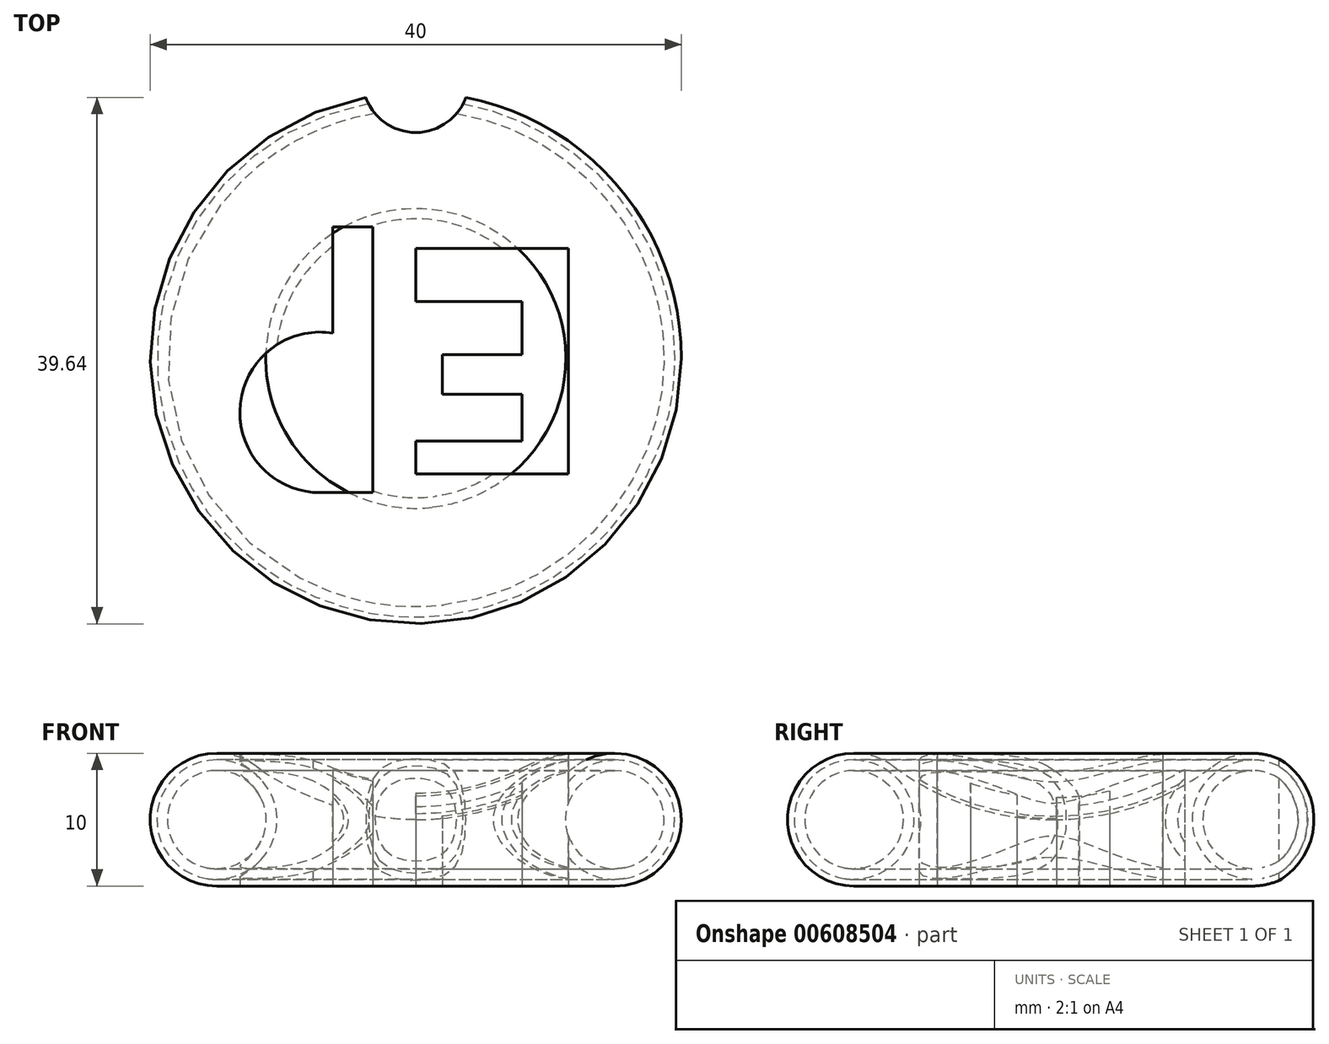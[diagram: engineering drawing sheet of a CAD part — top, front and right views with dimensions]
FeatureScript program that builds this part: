
annotation { "Feature Type Name" : "Feature", "Feature Type Description" : "" }
export const myFeature = defineFeature(function(context is Context, id is Id, definition is map)
    precondition{}
    {
        {
            var Q0;
            Q0=qCreatedBy(makeId("Front.planeOp"),FACE);
            var sketch = newSketch(context, id + "F0", { "sketchPlane" : qUnion([Q0])});
            skArc(sketch, "E0", {"start": v(-12, 9) * mm, "mid": v(-6.32, 6.03) * mm, "end": v(0, 5) * mm});
            skArc(sketch, "E1", {"start": v(-12, 9) * mm, "mid": v(-19.74, 6.58) * mm, "end": v(-15, 0) * mm});
            skLineSegment(sketch, "E2", {"start": v(0, 5) * mm, "end": v(0, 0) * mm});
            skLineSegment(sketch, "E3", {"start": v(0, 0) * mm, "end": v(-15, 0) * mm});
            skSolve(sketch);
        }
        {
            var Q0;
            Q0=makeQuery(id+"F0.imprint","IMPRINT",FACE,{"disambiguationData":[TD([[makeQuery(id+"F0.imprint","IMPRINT",EDGE,{"derivedFrom":sQuery(id+"F0.wireOp",EDGE,"E0")}),-1.0]])]});
            var Q1;
            Q1=sQuery(id+"F0.wireOp",EDGE,"E2");
            revolve(context, id + "F1", {"entities" : qUnion([Q0]), "axis" : qUnion([Q1]), "revolveType" : RevolveType.FULL});
        }
        {
            var Q0;
            Q0=makeQuery(id+"F1.opRevolve","SWEPT_FACE",FACE,{"disambiguationData":[OSD([sQuery(id+"F0.wireOp",EDGE,"E3")])]});
            var sketch = newSketch(context, id + "F2", { "sketchPlane" : qUnion([Q0])});
            skLineSegment(sketch, "E4", {"start": v(-3.25, -9.9) * mm, "end": v(-3.25, 10.1) * mm});
            skLineSegment(sketch, "E5", {"start": v(-3.25, 10.1) * mm, "end": v(-6.25, 10.1) * mm});
            skLineSegment(sketch, "E6", {"start": v(-6.25, -1.9) * mm, "end": v(-6.25, -9.9) * mm});
            skLineSegment(sketch, "E7", {"start": v(-3.25, -9.9) * mm, "end": v(-6.25, -9.9) * mm});
            skLineSegment(sketch, "E8", {"start": v(-6.25, 10.1) * mm, "end": v(-7.75, 10.1) * mm});
            skArc(sketch, "E9", {"start": v(-7.75, 10.1) * mm, "mid": v(-13.2, 3.32) * mm, "end": v(-6.25, -1.9) * mm});
            skLineSegment(sketch, "E10", {"start": v(11.5, 8.73) * mm, "end": v(11.5, -8.27) * mm});
            skLineSegment(sketch, "E11", {"start": v(0, -8.27) * mm, "end": v(11.5, -8.27) * mm});
            skLineSegment(sketch, "E12", {"start": v(0, -8.27) * mm, "end": v(0, -4.27) * mm});
            skLineSegment(sketch, "E13", {"start": v(0, -4.27) * mm, "end": v(8, -4.27) * mm});
            skLineSegment(sketch, "E14", {"start": v(8, -4.27) * mm, "end": v(8, -0.27) * mm});
            skLineSegment(sketch, "E15", {"start": v(8, -0.27) * mm, "end": v(2, -0.27) * mm});
            skLineSegment(sketch, "E16", {"start": v(2, 2.73) * mm, "end": v(2, -0.27) * mm});
            skLineSegment(sketch, "E17", {"start": v(2, 2.73) * mm, "end": v(8, 2.73) * mm});
            skLineSegment(sketch, "E18", {"start": v(8, 6.23) * mm, "end": v(8, 2.73) * mm});
            skLineSegment(sketch, "E19", {"start": v(8, 6.23) * mm, "end": v(0, 6.23) * mm});
            skLineSegment(sketch, "E20", {"start": v(11.5, 8.73) * mm, "end": v(0, 8.73) * mm});
            skLineSegment(sketch, "E21", {"start": v(0, 8.73) * mm, "end": v(0, 6.23) * mm});
            skPoint(sketch, "E22.orphan", {"position": v(0, -0.27) * mm});
            skSolve(sketch);
        }
        {
            var Q0;
            Q0=makeQuery(id+"F2.imprint","IMPRINT",FACE,{"disambiguationData":[TD([[makeQuery(id+"F2.imprint","IMPRINT",EDGE,{"derivedFrom":sQuery(id+"F2.wireOp",EDGE,"E4")}),1.0]])]});
            var Q1;
            Q1=makeQuery(id+"F2.imprint","IMPRINT",FACE,{"disambiguationData":[TD([[makeQuery(id+"F2.imprint","IMPRINT",EDGE,{"derivedFrom":sQuery(id+"F2.wireOp",EDGE,"bYQDJKkg-T13d-azlY-E3zt-dDLmTT6hyBzi")}),-1.0]])]});
            var Q2;
            {var subQ0=sQuery(id+"F2.wireOp",EDGE,"GuACwf4x-50aZ-0oHN-BAbR-x8a28NAcBo0e");var subQ1=sQuery(id+"F2.wireOp",EDGE,"7OYxP0y7-SmuM-tV8H-ZwjT-pEX8pjBidrrm");var subQ2=makeQuery(id+"F2.imprint","INTERSECT",VERTEX,{"derivedFrom":[subQ1,subQ0]});Q2=makeQuery(id+"F2.imprint","IMPRINT",FACE,{"disambiguationData":[TD([[makeQuery(id+"F2.imprint","IMPRINT",EDGE,{"disambiguationData":[TD([[subQ2,1.0]])],"derivedFrom":subQ1}),-1.0]])]});}
            extrude(context, id + "F3", {"entities" : qUnion([Q0, Q1, Q2]), "operationType" : NewBodyOperationType.REMOVE, "oppositeDirection" : true, "depth" : 25 * mm, "offsetDistance" : 25 * mm});
        }
        {
            var Q0;
            Q0=qCreatedBy(makeId("Front.planeOp"),FACE);
            var sketch = newSketch(context, id + "F4", { "sketchPlane" : qUnion([Q0])});
            skCircle(sketch, "E23", {"center": v(-15, 5) * mm, "radius": 4.5 * mm});
            skCircle(sketch, "E24", {"center": v(-15, 5) * mm, "radius": 3.7 * mm});
            skSolve(sketch);
        }
        {
            var Q0;
            Q0=sQuery(id+"F4.wireOp",EDGE,"E24");
            var Q1;
            Q1=sQuery(id+"F0.wireOp",EDGE,"E2");
            revolve(context, id + "F5", {"bodyType" : ToolBodyType.SURFACE, "surfaceEntities" : qUnion([Q0]), "axis" : qUnion([Q1]), "revolveType" : RevolveType.FULL});
        }
        {
            var Q0;
            Q0=qCreatedBy(makeId("Top.planeOp"),FACE);
            var sketch = newSketch(context, id + "F6", { "sketchPlane" : qUnion([Q0])});
            skCircle(sketch, "E25", {"center": v(0, 21) * mm, "radius": 4 * mm});
            skSolve(sketch);
        }
        {
            var Q0;
            Q0=makeQuery(id+"F6.imprint","IMPRINT",FACE,{"disambiguationData":[TD([[makeQuery(id+"F6.imprint","IMPRINT",EDGE,{"derivedFrom":sQuery(id+"F6.wireOp",EDGE,"E25")}),1.0]])]});
            extrude(context, id + "F7", {"entities" : qUnion([Q0]), "operationType" : NewBodyOperationType.REMOVE, "depth" : 25 * mm, "offsetDistance" : 25 * mm});
        }
        {
            var Q0;
            Q0=makeQuery(id+"F5.opRevolve","SWEPT_BODY",BODY,{"disambiguationData":[OSD([sQuery(id+"F4.wireOp",EDGE,"E24")])]});
            deleteBodies(context, id + "F8", {"entities" : qUnion([Q0])});
        }
        {
            var Q0;
            Q0 = qSketchRegion(id + "F2", true);
            extrude(context, id + "F9", {"entities" : qUnion([Q0]), "operationType" : NewBodyOperationType.REMOVE, "oppositeDirection" : true, "depth" : 25 * mm, "offsetDistance" : 25 * mm});
        }
        {
            var Q0;
            Q0=sQuery(id+"F4.wireOp",EDGE,"E24");
            var Q1;
            Q1=sQuery(id+"F0.wireOp",EDGE,"E2");
            revolve(context, id + "F10", {"bodyType" : ToolBodyType.SURFACE, "surfaceEntities" : qUnion([Q0]), "axis" : qUnion([Q1]), "revolveType" : RevolveType.FULL});
        }
        {
            var Q0;
            Q0=makeQuery(id+"F10.opRevolve","SWEPT_BODY",BODY,{"disambiguationData":[OSD([sQuery(id+"F4.wireOp",EDGE,"E24")])]});
            deleteBodies(context, id + "F11", {"entities" : qUnion([Q0])});
        }
        {
            var Q0;
            Q0 = qSketchRegion(id + "F4", true);
            var Q1;
            Q1=sQuery(id+"F4.wireOp",EDGE,"E24");
            var Q2;
            Q2=sQuery(id+"F0.wireOp",EDGE,"E2");
            revolve(context, id + "F12", {"operationType" : NewBodyOperationType.REMOVE, "entities" : qUnion([Q0]), "surfaceEntities" : qUnion([Q1]), "axis" : qUnion([Q2]), "revolveType" : RevolveType.FULL, "oppositeDirection" : true});
        }
        {
            var Q0;
            Q0=makeQuery(id+"F12.boolean.opBoolean","SPLIT",FACE,{"disambiguationData":[TD([makeQuery(id+"F12.opRevolve","SWEPT_FACE",FACE,{"disambiguationData":[OSD([sQuery(id+"F4.wireOp",EDGE,"E24")])]})])],"derivedFrom":makeQuery(id+"F9.boolean.opBoolean","COPY",FACE,{"derivedFrom":makeQuery(id+"F9.opExtrude","SWEPT_FACE",FACE,{"disambiguationData":[OSD([sQuery(id+"F2.wireOp",EDGE,"E20")])]})})});
            var Q1;
            Q1=sQuery(id+"F0.wireOp",EDGE,"E2");
            revolve(context, id + "F13", {"operationType" : NewBodyOperationType.ADD, "entities" : qUnion([Q0]), "axis" : qUnion([Q1]), "revolveType" : RevolveType.FULL});
        }
    });
